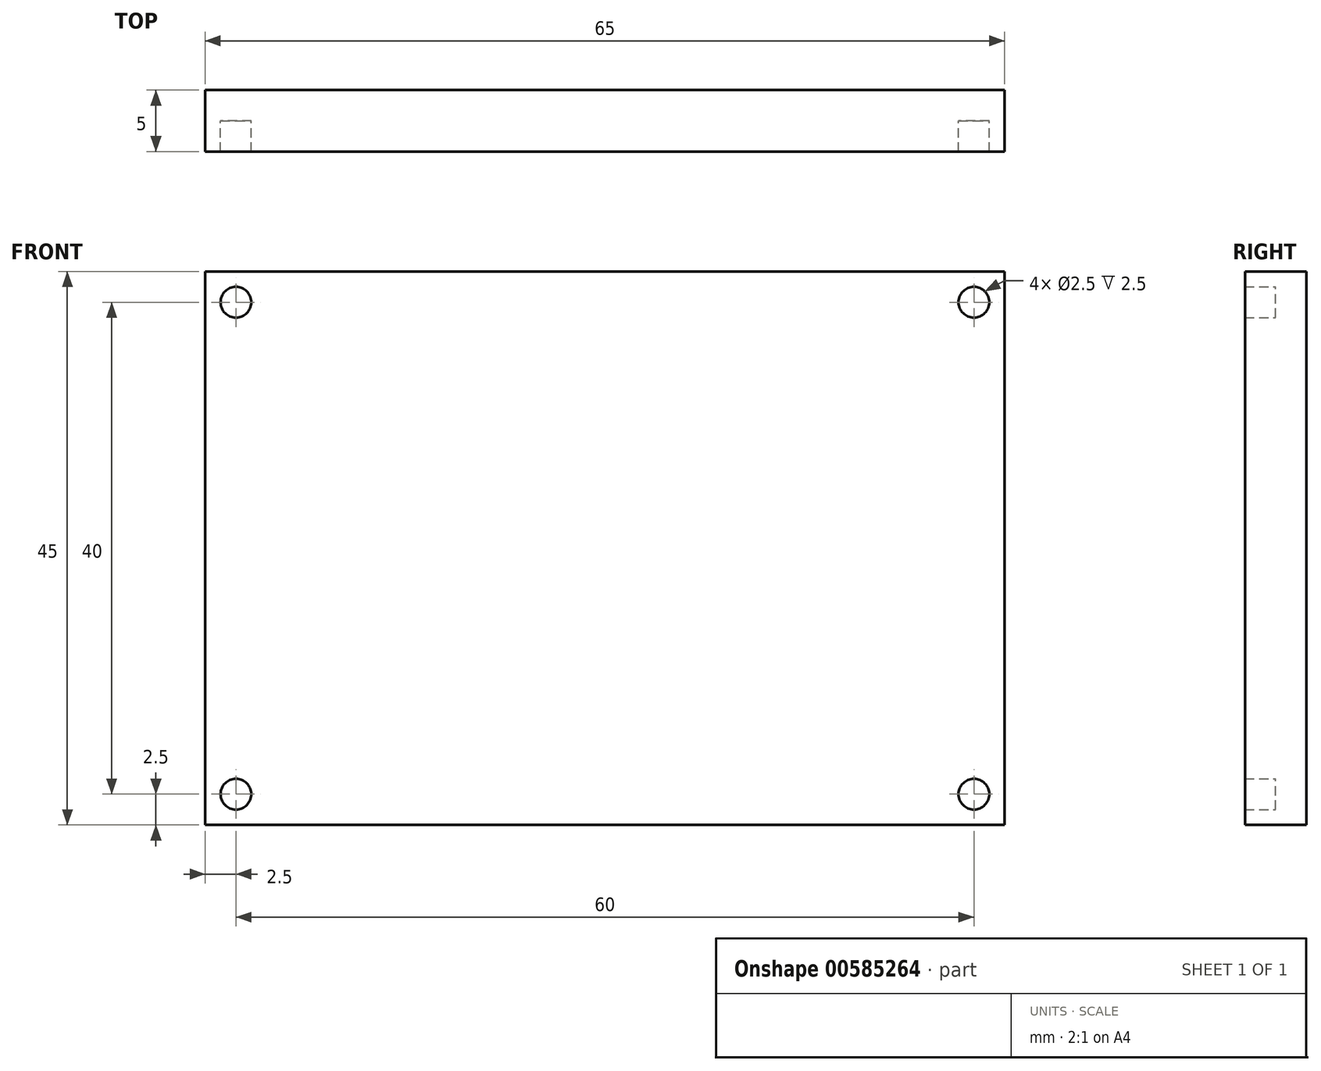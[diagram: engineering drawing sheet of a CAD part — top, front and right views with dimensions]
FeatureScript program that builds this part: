
annotation { "Feature Type Name" : "Feature", "Feature Type Description" : "" }
export const myFeature = defineFeature(function(context is Context, id is Id, definition is map)
    precondition{}
    {
        {
            var Q0;
            Q0=qCreatedBy(makeId("Front.planeOp"),FACE);
            var sketch = newSketch(context, id + "F0", { "sketchPlane" : qUnion([Q0])});
            skLineSegment(sketch, "E0.bottom", {"start": v(0, 0) * mm, "end": v(65, 0) * mm});
            skLineSegment(sketch, "E0.top", {"start": v(0, 45) * mm, "end": v(65, 45) * mm});
            skLineSegment(sketch, "E0.left", {"start": v(0, 0) * mm, "end": v(0, 45) * mm});
            skLineSegment(sketch, "E0.right", {"start": v(65, 0) * mm, "end": v(65, 45) * mm});
            skCircle(sketch, "E1", {"center": v(2.5, 42.5) * mm, "radius": 1.25 * mm});
            skCircle(sketch, "E2", {"center": v(62.5, 42.5) * mm, "radius": 1.25 * mm});
            skCircle(sketch, "E3", {"center": v(2.5, 2.5) * mm, "radius": 1.25 * mm});
            skCircle(sketch, "E4", {"center": v(62.5, 2.5) * mm, "radius": 1.25 * mm});
            skSolve(sketch);
        }
        {
            var Q0;
            Q0 = qSketchRegion(id + "F0", true);
            extrude(context, id + "F1", {"entities" : qUnion([Q0]), "depth" : 5 * mm, "offsetDistance" : 25 * mm});
        }
        {
            var Q0;
            Q0=makeQuery(id+"F0.imprint","IMPRINT",FACE,{"disambiguationData":[TD([[makeQuery(id+"F0.imprint","IMPRINT",EDGE,{"derivedFrom":sQuery(id+"F0.wireOp",EDGE,"E1")}),1.0]])]});
            var Q1;
            Q1=makeQuery(id+"F0.imprint","IMPRINT",FACE,{"disambiguationData":[TD([[makeQuery(id+"F0.imprint","IMPRINT",EDGE,{"derivedFrom":sQuery(id+"F0.wireOp",EDGE,"E3")}),1.0]])]});
            var Q2;
            Q2=makeQuery(id+"F0.imprint","IMPRINT",FACE,{"disambiguationData":[TD([[makeQuery(id+"F0.imprint","IMPRINT",EDGE,{"derivedFrom":sQuery(id+"F0.wireOp",EDGE,"E4")}),1.0]])]});
            var Q3;
            Q3=makeQuery(id+"F0.imprint","IMPRINT",FACE,{"disambiguationData":[TD([[makeQuery(id+"F0.imprint","IMPRINT",EDGE,{"derivedFrom":sQuery(id+"F0.wireOp",EDGE,"E2")}),1.0]])]});
            extrude(context, id + "F2", {"entities" : qUnion([Q0, Q1, Q2, Q3]), "operationType" : NewBodyOperationType.ADD, "depth" : 2.5 * mm, "offsetDistance" : 25 * mm});
        }
    });
